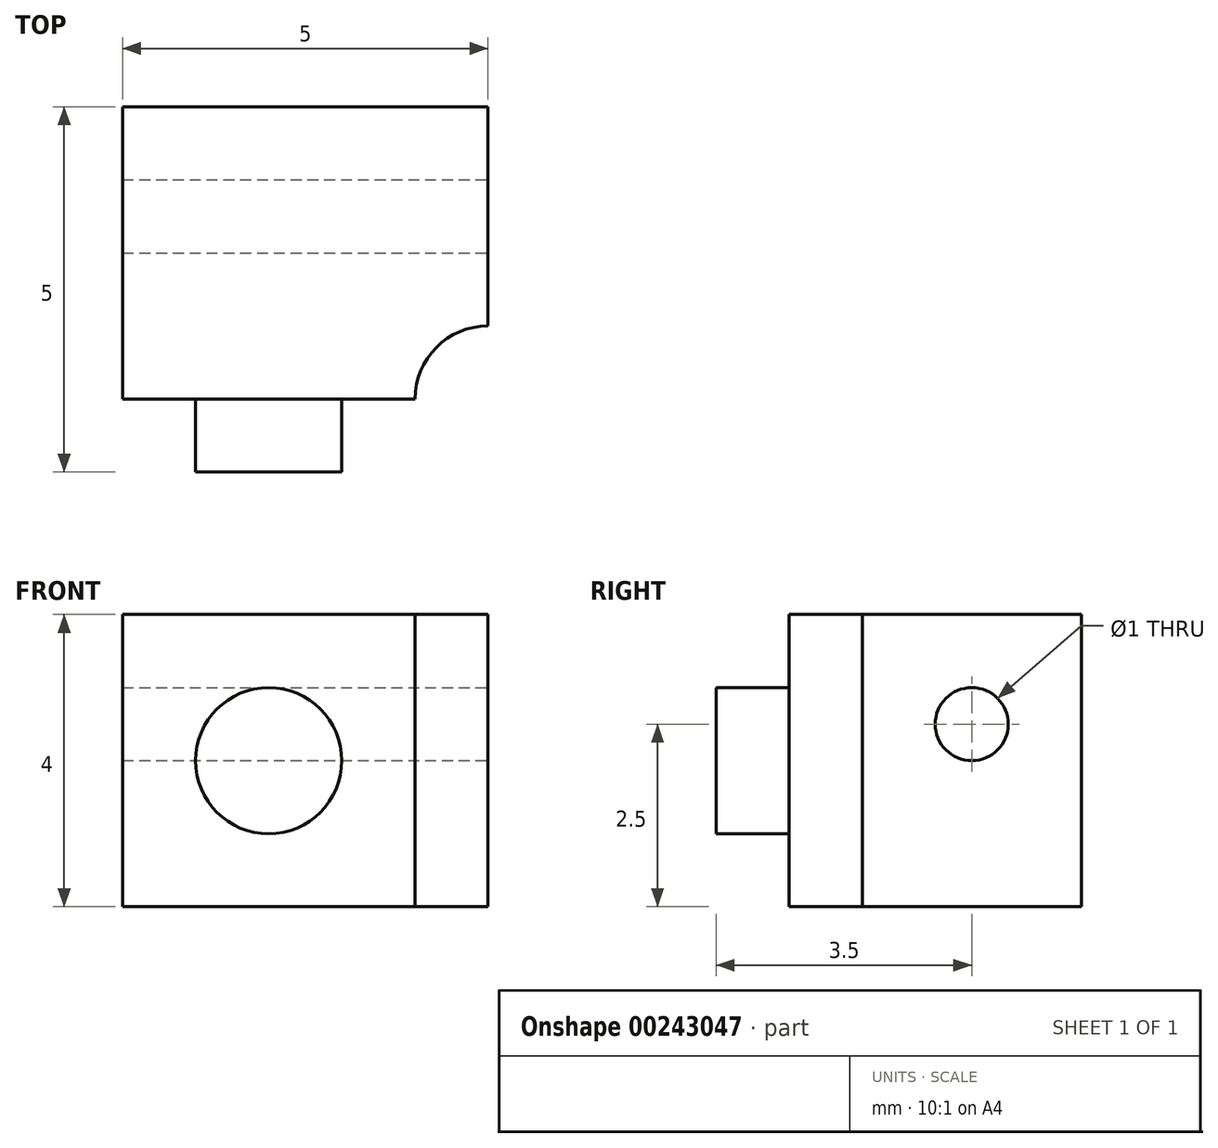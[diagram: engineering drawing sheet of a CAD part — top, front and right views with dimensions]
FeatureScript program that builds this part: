
annotation { "Feature Type Name" : "Feature", "Feature Type Description" : "" }
export const myFeature = defineFeature(function(context is Context, id is Id, definition is map)
    precondition{}
    {
        {
            var Q0;
            Q0=qCreatedBy(makeId("Top.planeOp"),FACE);
            var sketch = newSketch(context, id + "F0", { "sketchPlane" : qUnion([Q0])});
            skLineSegment(sketch, "E0.bottom", {"start": v(0, 0) * mm, "end": v(5, 0) * mm});
            skLineSegment(sketch, "E0.top", {"start": v(0, 4) * mm, "end": v(5, 4) * mm});
            skLineSegment(sketch, "E0.left", {"start": v(0, 0) * mm, "end": v(0, 4) * mm});
            skLineSegment(sketch, "E0.right", {"start": v(5, 0) * mm, "end": v(5, 4) * mm});
            skSolve(sketch);
        }
        {
            var Q0;
            Q0 = qSketchRegion(id + "F0", true);
            extrude(context, id + "F1", {"entities" : qUnion([Q0]), "depth" : 4 * mm});
        }
        {
            var Q0;
            Q0=makeQuery(id+"F1.opExtrude","SWEPT_FACE",FACE,{"disambiguationData":[OSD([sQuery(id+"F0.wireOp",EDGE,"E0.right")])]});
            var sketch = newSketch(context, id + "F2", { "sketchPlane" : qUnion([Q0])});
            skSolve(sketch);
        }
        {
            var Q0;
            {var subQ0=sQuery(id+"F0.wireOp",EDGE,"E0.right");Q0=makeQuery(id+"F2.imprint","IMPRINT",FACE,{"disambiguationData":[TD([[makeQuery(id+"F2.imprint","IMPRINT",EDGE,{"derivedFrom":makeQuery(id+"F1.opExtrude","CAP_EDGE",EDGE,{"disambiguationData":[OSD([subQ0])],"isStart":true})}),1.0]])]});}
            var sketch = newSketch(context, id + "F3", { "sketchPlane" : qUnion([Q0])});
            skPoint(sketch, "E1.0", {"position": v(4, 4) * mm});
            skPoint(sketch, "E2.0", {"position": v(0, 0) * mm});
            skLineSegment(sketch, "E3", {"start": v(4, 4) * mm, "end": v(0, 0) * mm, "construction": true});
            skSolve(sketch);
        }
        {
            var Q0;
            Q0=makeQuery(id+"F1.opExtrude","CAP_FACE",FACE,{"disambiguationData":[OSD([sQuery(id+"F0.wireOp",EDGE,"E0.bottom"),sQuery(id+"F0.wireOp",EDGE,"E0.top"),sQuery(id+"F0.wireOp",EDGE,"E0.left"),sQuery(id+"F0.wireOp",EDGE,"E0.right")])],"isStart":false});
            var sketch = newSketch(context, id + "F4", { "sketchPlane" : qUnion([Q0])});
            skCircle(sketch, "E4", {"center": v(5, 0) * mm, "radius": 1 * mm});
            skSolve(sketch);
        }
        {
            var Q0;
            Q0 = qSketchRegion(id + "F4", true);
            extrude(context, id + "F5", {"entities" : qUnion([Q0]), "operationType" : NewBodyOperationType.REMOVE, "oppositeDirection" : true, "depth" : 25 * mm});
        }
        {
            var Q0;
            Q0=makeQuery(id+"F1.opExtrude","SWEPT_FACE",FACE,{"disambiguationData":[OSD([sQuery(id+"F0.wireOp",EDGE,"E0.bottom")])]});
            var sketch = newSketch(context, id + "F6", { "sketchPlane" : qUnion([Q0])});
            skCircle(sketch, "E5", {"center": v(2, 2) * mm, "radius": 1 * mm});
            skPoint(sketch, "E5.centerSnap0", {"position": v(0, 2) * mm});
            skPoint(sketch, "E5.centerSnap1", {"position": v(2, 4) * mm});
            skSolve(sketch);
        }
        {
            var Q0;
            Q0 = qSketchRegion(id + "F6", true);
            extrude(context, id + "F7", {"entities" : qUnion([Q0]), "operationType" : NewBodyOperationType.ADD, "depth" : 1 * mm});
        }
        {
            var Q0;
            Q0=makeQuery(id+"F1.opExtrude","SWEPT_FACE",FACE,{"disambiguationData":[OSD([sQuery(id+"F0.wireOp",EDGE,"E0.right")])]});
            var sketch = newSketch(context, id + "F8", { "sketchPlane" : qUnion([Q0])});
            skLineSegment(sketch, "E6.0", {"start": v(4, 4) * mm, "end": v(0, 0) * mm});
            skCircle(sketch, "E7", {"center": v(2.5, 2.5) * mm, "radius": 0.5 * mm});
            skPoint(sketch, "E7.centerSnap0", {"position": v(2.5, 4) * mm});
            skSolve(sketch);
        }
        {
            var Q0;
            Q0 = qSketchRegion(id + "F8", true);
            extrude(context, id + "F9", {"entities" : qUnion([Q0]), "operationType" : NewBodyOperationType.REMOVE, "oppositeDirection" : true, "depth" : 25 * mm});
        }
    });
